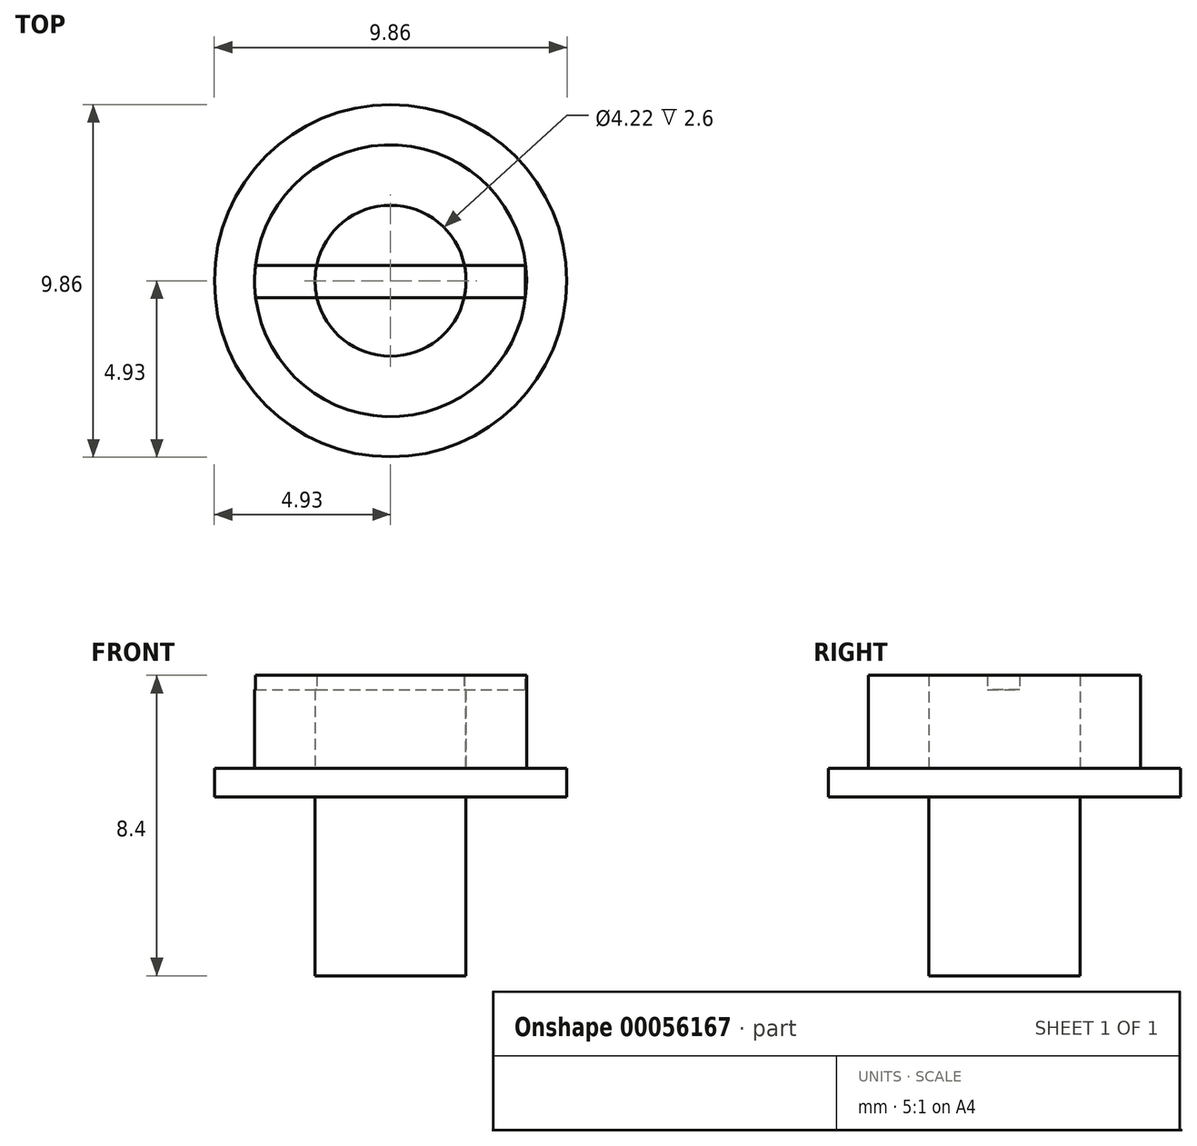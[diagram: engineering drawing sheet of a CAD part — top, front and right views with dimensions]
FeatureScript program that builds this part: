
annotation { "Feature Type Name" : "Feature", "Feature Type Description" : "" }
export const myFeature = defineFeature(function(context is Context, id is Id, definition is map)
    precondition{}
    {
        {
            var Q0;
            Q0=qCreatedBy(makeId("Top.planeOp"),FACE);
            var sketch = newSketch(context, id + "F0", { "sketchPlane" : qUnion([Q0])});
            skCircle(sketch, "E0", {"center": v(0, 0) * mm, "radius": 2.1 * mm});
            skSolve(sketch);
        }
        {
            var Q0;
            Q0=makeQuery(id+"F0.imprint","IMPRINT",FACE,{"disambiguationData":[TD([[makeQuery(id+"F0.imprint","IMPRINT",EDGE,{"derivedFrom":sQuery(id+"F0.wireOp",EDGE,"E0")}),1.0]])]});
            extrude(context, id + "F1", {"entities" : qUnion([Q0]), "depth" : 5.8 * mm});
        }
        {
            var Q0;
            Q0=makeQuery(id+"F1.opExtrude","CAP_FACE",FACE,{"disambiguationData":[OSD([sQuery(id+"F0.wireOp",EDGE,"E0")])],"isStart":false});
            var sketch = newSketch(context, id + "F2", { "sketchPlane" : qUnion([Q0])});
            skCircle(sketch, "E1", {"center": v(0, 0) * mm, "radius": 4.92 * mm});
            skSolve(sketch);
        }
        {
            var Q0;
            Q0=makeQuery(id+"F2.imprint","IMPRINT",FACE,{"disambiguationData":[TD([[makeQuery(id+"F2.imprint","IMPRINT",EDGE,{"derivedFrom":sQuery(id+"F2.wireOp",EDGE,"E1")}),1.0]])]});
            extrude(context, id + "F3", {"entities" : qUnion([Q0]), "oppositeDirection" : true, "depth" : .8 * mm});
        }
        {
            var Q0;
            Q0=makeQuery(id+"F1.opExtrude","CAP_FACE",FACE,{"disambiguationData":[OSD([sQuery(id+"F0.wireOp",EDGE,"E0")])],"isStart":false});
            var sketch = newSketch(context, id + "F4", { "sketchPlane" : qUnion([Q0])});
            skCircle(sketch, "E2", {"center": v(0, 0) * mm, "radius": 3.8 * mm});
            skSolve(sketch);
        }
        {
            var Q0;
            Q0=makeQuery(id+"F4.imprint","IMPRINT",FACE,{"disambiguationData":[TD([[makeQuery(id+"F4.imprint","IMPRINT",EDGE,{"derivedFrom":sQuery(id+"F4.wireOp",EDGE,"E2")}),1.0]])]});
            extrude(context, id + "F5", {"entities" : qUnion([Q0]), "operationType" : NewBodyOperationType.ADD, "depth" : 2.6 * mm});
        }
        {
            var Q0;
            Q0=makeQuery(id+"F1.opExtrude","CAP_FACE",FACE,{"disambiguationData":[OSD([sQuery(id+"F0.wireOp",EDGE,"E0")])],"isStart":false});
            var sketch = newSketch(context, id + "F6", { "sketchPlane" : qUnion([Q0])});
            skCircle(sketch, "E3", {"center": v(0, 0) * mm, "radius": 2.1 * mm});
            skSolve(sketch);
        }
        {
            var Q0;
            Q0=makeQuery(id+"F6.imprint","IMPRINT",FACE,{"disambiguationData":[TD([[makeQuery(id+"F6.imprint","IMPRINT",EDGE,{"derivedFrom":sQuery(id+"F6.wireOp",EDGE,"E3")}),1.0]])]});
            extrude(context, id + "F7", {"entities" : qUnion([Q0]), "depth" : 2.6 * mm});
        }
        {
            var Q0;
            Q0=makeQuery(id+"F7.opExtrude","CAP_FACE",FACE,{"disambiguationData":[OSD([sQuery(id+"F6.wireOp",EDGE,"E3")])],"isStart":false});
            var sketch = newSketch(context, id + "F8", { "sketchPlane" : qUnion([Q0])});
            skLineSegment(sketch, "E4.bottom", {"start": v(-3.8, 0.43) * mm, "end": v(3.76, 0.43) * mm});
            skLineSegment(sketch, "E4.top", {"start": v(-3.8, -0.47) * mm, "end": v(3.76, -0.47) * mm});
            skLineSegment(sketch, "E4.left", {"start": v(-3.8, 0.43) * mm, "end": v(-3.8, -0.47) * mm});
            skLineSegment(sketch, "E4.right", {"start": v(3.76, 0.43) * mm, "end": v(3.76, -0.47) * mm});
            skSolve(sketch);
        }
        {
            var Q0;
            {var subQ0=sQuery(id+"F8.wireOp",EDGE,"E4.left");Q0=makeQuery(id+"F8.imprint","IMPRINT",FACE,{"disambiguationData":[TD([[makeQuery(id+"F8.imprint","IMPRINT",EDGE,{"derivedFrom":subQ0}),1.0]])]});}
            var Q1;
            {var subQ0=sQuery(id+"F8.wireOp",EDGE,"E4.bottom");var subQ1=makeQuery(id+"F7.opExtrude","CAP_EDGE",EDGE,{"disambiguationData":[OSD([sQuery(id+"F6.wireOp",EDGE,"E3")])],"isStart":false});var subQ2=makeQuery(id+"F8.imprint","INTERSECT",VERTEX,{"disambiguationData":[OD(0.0)],"derivedFrom":[subQ1,subQ0]});Q1=makeQuery(id+"F8.imprint","IMPRINT",FACE,{"disambiguationData":[TD([[makeQuery(id+"F8.imprint","IMPRINT",EDGE,{"disambiguationData":[TD([[subQ2,-1.0]])],"derivedFrom":subQ0}),-1.0]])]});}
            var Q2;
            {var subQ0=sQuery(id+"F8.wireOp",EDGE,"E4.right");Q2=makeQuery(id+"F8.imprint","IMPRINT",FACE,{"disambiguationData":[TD([[makeQuery(id+"F8.imprint","IMPRINT",EDGE,{"derivedFrom":subQ0}),-1.0]])]});}
            extrude(context, id + "F9", {"entities" : qUnion([Q0, Q1, Q2]), "operationType" : NewBodyOperationType.REMOVE, "oppositeDirection" : true, "depth" : .4 * mm});
        }
    });
